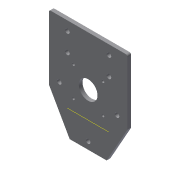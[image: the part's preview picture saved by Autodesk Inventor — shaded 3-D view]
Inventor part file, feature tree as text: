
AUTODESK INVENTOR PART (.ipt)
format: ipt  version: 2019.4 (Build 234330000, 330)  size: 135,168 bytes
history: native  units: mm
features: extrude x1, fillet x1, mirror x1, plane x1, sketch x1
ambient origin geometry x8: Origin, YZ Plane, XZ Plane, XY Plane, X Axis, Y Axis, Z Axis, Center Point
bodies: Solid1 (feature_tree)
feature tree (5):
  extrude  "Extrusion1"  Depth=2.0mm
  fillet  "Fillet1"  Radius=70.0mm
  mirror  "Mirror1"
  plane  "Work Plane1"
  sketch  "Sketch1"  dims[d0=20.0mm d1=42.5mm d2=40.0mm d3=70.0mm d4=4.9mm d5=4.9mm d6=32.0mm d7=32.0mm d8=8.0mm d9=40.0mm d10=8.0mm d11=2.9mm d12=2.8mm d13=4.9mm d14=4.9mm d15=10.0mm d16=30.0mm d17=20.0mm d18=20.0mm d19=4.0mm d20=0.0mm d21=2.0mm d22=-28.0mm]
